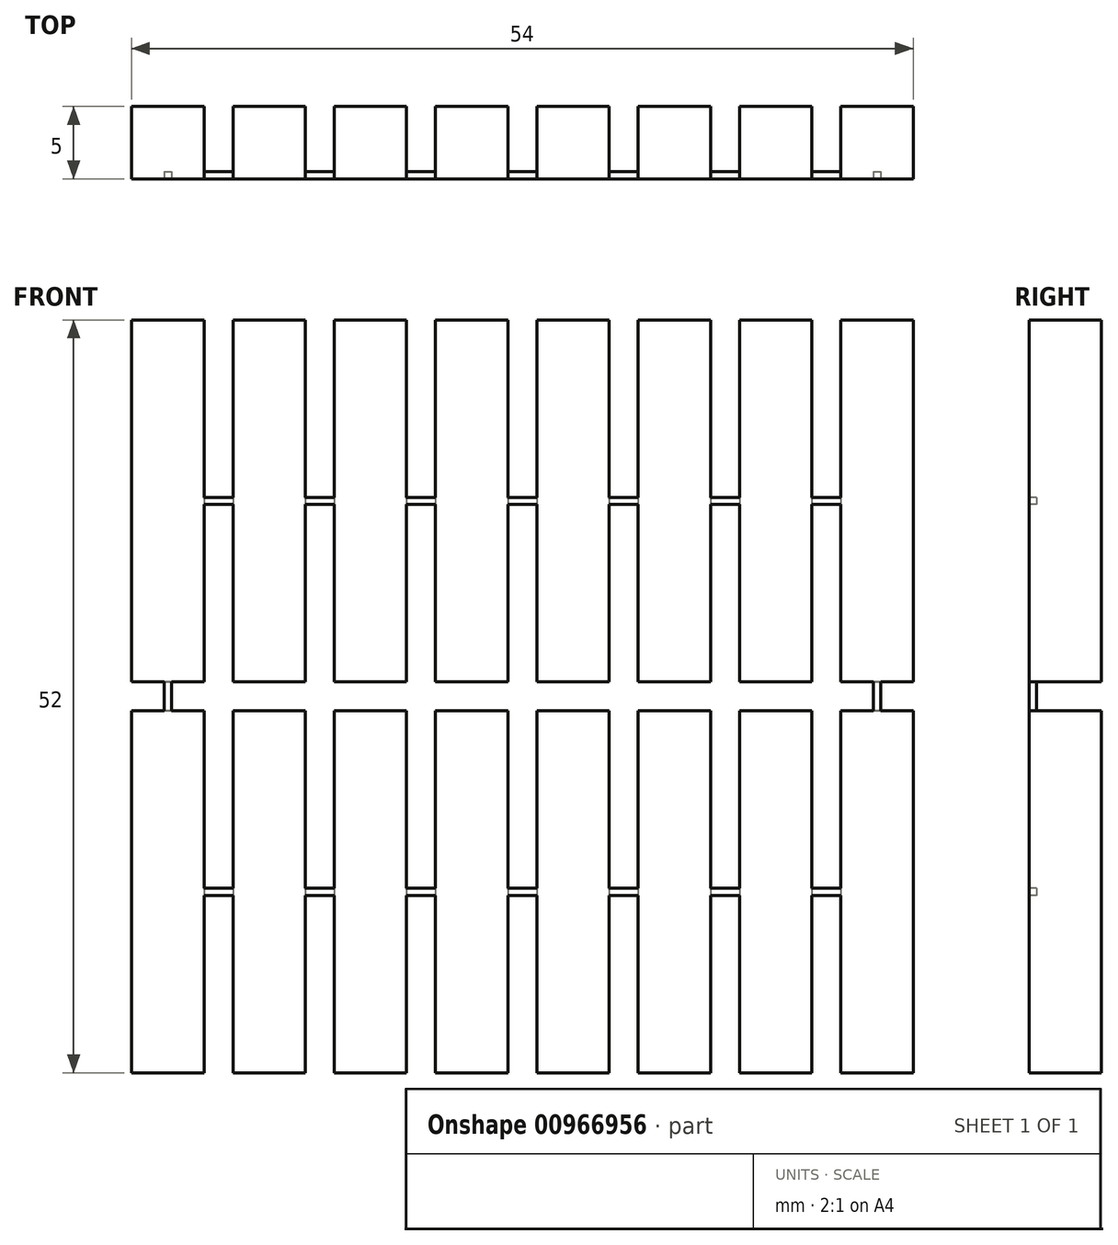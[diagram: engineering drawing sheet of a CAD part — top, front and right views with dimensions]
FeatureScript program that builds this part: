
annotation { "Feature Type Name" : "Feature", "Feature Type Description" : "" }
export const myFeature = defineFeature(function(context is Context, id is Id, definition is map)
    precondition{}
    {
        {
            var Q0;
            Q0=qCreatedBy(makeId("Front.planeOp"),FACE);
            var sketch = newSketch(context, id + "F0", { "sketchPlane" : qUnion([Q0])});
            skLineSegment(sketch, "E0.bottom", {"start": v(2.5, -12.5) * mm, "end": v(-2.5, -12.5) * mm});
            skLineSegment(sketch, "E0.top", {"start": v(2.5, 12.5) * mm, "end": v(-2.5, 12.5) * mm});
            skLineSegment(sketch, "E0.left", {"start": v(2.5, -12.5) * mm, "end": v(2.5, 12.5) * mm});
            skLineSegment(sketch, "E0.right", {"start": v(-2.5, -12.5) * mm, "end": v(-2.5, 12.5) * mm});
            skPoint(sketch, "E0.middle", {"position": v(0, 0) * mm});
            skLineSegment(sketch, "E1.top", {"start": v(0.25, 14.5) * mm, "end": v(-0.25, 14.5) * mm});
            skPoint(sketch, "E1.middle", {"position": v(0, 12.5) * mm});
            skLineSegment(sketch, "E2", {"start": v(-0.25, 14.5) * mm, "end": v(-0.25, 12.5) * mm});
            skLineSegment(sketch, "E3", {"start": v(0.25, 14.5) * mm, "end": v(0.25, 12.5) * mm});
            skLineSegment(sketch, "E4", {"start": v(0.25, 12.5) * mm, "end": v(-0.25, 12.5) * mm});
            skPoint(sketch, "E5", {"position": v(0, 14.5) * mm});
            skPoint(sketch, "E6", {"position": v(2.5, 0) * mm});
            skLineSegment(sketch, "E7.right", {"start": v(4.5, -0.25) * mm, "end": v(4.5, 0.25) * mm});
            skLineSegment(sketch, "E8", {"start": v(4.5, 0.25) * mm, "end": v(2.5, 0.25) * mm});
            skLineSegment(sketch, "E9", {"start": v(4.5, -0.25) * mm, "end": v(2.5, -0.25) * mm});
            skLineSegment(sketch, "E10", {"start": v(2.5, -0.25) * mm, "end": v(2.5, 0.25) * mm});
            skPoint(sketch, "E11", {"position": v(4.5, 0) * mm});
            skLineSegment(sketch, "E12.0.1.0", {"start": v(4.5, 27.25) * mm, "end": v(2.5, 27.25) * mm});
            skLineSegment(sketch, "E12.0.1.1", {"start": v(2.5, 14.5) * mm, "end": v(2.5, 39.5) * mm});
            skLineSegment(sketch, "E12.0.1.2", {"start": v(0.25, 41.5) * mm, "end": v(0.25, 39.5) * mm});
            skPoint(sketch, "E12.0.1.3", {"position": v(2.5, 27) * mm});
            skLineSegment(sketch, "E12.0.1.4", {"start": v(-0.25, 41.5) * mm, "end": v(-0.25, 39.5) * mm});
            skLineSegment(sketch, "E12.0.1.5", {"start": v(2.5, 39.5) * mm, "end": v(-2.5, 39.5) * mm});
            skPoint(sketch, "E12.0.1.6", {"position": v(0, 27) * mm});
            skLineSegment(sketch, "E12.0.1.7", {"start": v(2.5, 14.5) * mm, "end": v(-2.5, 14.5) * mm});
            skLineSegment(sketch, "E12.0.1.8", {"start": v(4.5, 26.75) * mm, "end": v(2.5, 26.75) * mm});
            skPoint(sketch, "E12.0.1.9", {"position": v(4.5, 27) * mm});
            skLineSegment(sketch, "E12.0.1.10", {"start": v(-2.5, 14.5) * mm, "end": v(-2.5, 39.5) * mm});
            skPoint(sketch, "E12.0.1.11", {"position": v(0, 39.5) * mm});
            skPoint(sketch, "E12.0.1.12", {"position": v(0, 41.5) * mm});
            skPoint(sketch, "E12.0.1.13", {"position": v(4.5, 27) * mm});
            skPoint(sketch, "E12.0.1.14", {"position": v(0, 41.5) * mm});
            skPoint(sketch, "E12.0.1.15", {"position": v(2.5, 27) * mm});
            skLineSegment(sketch, "E12.0.1.16", {"start": v(0.25, 41.5) * mm, "end": v(-0.25, 41.5) * mm});
            skLineSegment(sketch, "E12.0.1.17", {"start": v(4.5, 26.75) * mm, "end": v(4.5, 27.25) * mm});
            skLineSegment(sketch, "E12.0.1.18", {"start": v(2.5, 26.75) * mm, "end": v(2.5, 27.25) * mm});
            skLineSegment(sketch, "E12.0.1.19", {"start": v(0.25, 39.5) * mm, "end": v(-0.25, 39.5) * mm});
            skLineSegment(sketch, "E12.1.0.0", {"start": v(11.5, 0.25) * mm, "end": v(9.5, 0.25) * mm});
            skLineSegment(sketch, "E12.1.0.1", {"start": v(9.5, -12.5) * mm, "end": v(9.5, 12.5) * mm});
            skLineSegment(sketch, "E12.1.0.2", {"start": v(7.25, 14.5) * mm, "end": v(7.25, 12.5) * mm});
            skPoint(sketch, "E12.1.0.3", {"position": v(9.5, 0) * mm});
            skLineSegment(sketch, "E12.1.0.4", {"start": v(6.75, 14.5) * mm, "end": v(6.75, 12.5) * mm});
            skLineSegment(sketch, "E12.1.0.5", {"start": v(9.5, 12.5) * mm, "end": v(4.5, 12.5) * mm});
            skPoint(sketch, "E12.1.0.6", {"position": v(7, 0) * mm});
            skLineSegment(sketch, "E12.1.0.7", {"start": v(9.5, -12.5) * mm, "end": v(4.5, -12.5) * mm});
            skLineSegment(sketch, "E12.1.0.8", {"start": v(11.5, -0.25) * mm, "end": v(9.5, -0.25) * mm});
            skPoint(sketch, "E12.1.0.9", {"position": v(11.5, 0) * mm});
            skLineSegment(sketch, "E12.1.0.10", {"start": v(4.5, -12.5) * mm, "end": v(4.5, 12.5) * mm});
            skPoint(sketch, "E12.1.0.11", {"position": v(7, 12.5) * mm});
            skPoint(sketch, "E12.1.0.12", {"position": v(7, 14.5) * mm});
            skPoint(sketch, "E12.1.0.13", {"position": v(11.5, 0) * mm});
            skPoint(sketch, "E12.1.0.14", {"position": v(7, 14.5) * mm});
            skPoint(sketch, "E12.1.0.15", {"position": v(9.5, 0) * mm});
            skLineSegment(sketch, "E12.1.0.16", {"start": v(7.25, 14.5) * mm, "end": v(6.75, 14.5) * mm});
            skLineSegment(sketch, "E12.1.0.17", {"start": v(11.5, -0.25) * mm, "end": v(11.5, 0.25) * mm});
            skLineSegment(sketch, "E12.1.0.18", {"start": v(9.5, -0.25) * mm, "end": v(9.5, 0.25) * mm});
            skLineSegment(sketch, "E12.1.0.19", {"start": v(7.25, 12.5) * mm, "end": v(6.75, 12.5) * mm});
            skLineSegment(sketch, "E12.1.1.0", {"start": v(11.5, 27.25) * mm, "end": v(9.5, 27.25) * mm});
            skLineSegment(sketch, "E12.1.1.1", {"start": v(9.5, 14.5) * mm, "end": v(9.5, 39.5) * mm});
            skLineSegment(sketch, "E12.1.1.2", {"start": v(7.25, 41.5) * mm, "end": v(7.25, 39.5) * mm});
            skPoint(sketch, "E12.1.1.3", {"position": v(9.5, 27) * mm});
            skLineSegment(sketch, "E12.1.1.4", {"start": v(6.75, 41.5) * mm, "end": v(6.75, 39.5) * mm});
            skLineSegment(sketch, "E12.1.1.5", {"start": v(9.5, 39.5) * mm, "end": v(4.5, 39.5) * mm});
            skPoint(sketch, "E12.1.1.6", {"position": v(7, 27) * mm});
            skLineSegment(sketch, "E12.1.1.7", {"start": v(9.5, 14.5) * mm, "end": v(4.5, 14.5) * mm});
            skLineSegment(sketch, "E12.1.1.8", {"start": v(11.5, 26.75) * mm, "end": v(9.5, 26.75) * mm});
            skPoint(sketch, "E12.1.1.9", {"position": v(11.5, 27) * mm});
            skLineSegment(sketch, "E12.1.1.10", {"start": v(4.5, 14.5) * mm, "end": v(4.5, 39.5) * mm});
            skPoint(sketch, "E12.1.1.11", {"position": v(7, 39.5) * mm});
            skPoint(sketch, "E12.1.1.12", {"position": v(7, 41.5) * mm});
            skPoint(sketch, "E12.1.1.13", {"position": v(11.5, 27) * mm});
            skPoint(sketch, "E12.1.1.14", {"position": v(7, 41.5) * mm});
            skPoint(sketch, "E12.1.1.15", {"position": v(9.5, 27) * mm});
            skLineSegment(sketch, "E12.1.1.16", {"start": v(7.25, 41.5) * mm, "end": v(6.75, 41.5) * mm});
            skLineSegment(sketch, "E12.1.1.17", {"start": v(11.5, 26.75) * mm, "end": v(11.5, 27.25) * mm});
            skLineSegment(sketch, "E12.1.1.18", {"start": v(9.5, 26.75) * mm, "end": v(9.5, 27.25) * mm});
            skLineSegment(sketch, "E12.1.1.19", {"start": v(7.25, 39.5) * mm, "end": v(6.75, 39.5) * mm});
            skLineSegment(sketch, "E12.2.0.0", {"start": v(18.5, 0.25) * mm, "end": v(16.5, 0.25) * mm});
            skLineSegment(sketch, "E12.2.0.1", {"start": v(16.5, -12.5) * mm, "end": v(16.5, 12.5) * mm});
            skLineSegment(sketch, "E12.2.0.2", {"start": v(14.25, 14.5) * mm, "end": v(14.25, 12.5) * mm});
            skPoint(sketch, "E12.2.0.3", {"position": v(16.5, 0) * mm});
            skLineSegment(sketch, "E12.2.0.4", {"start": v(13.75, 14.5) * mm, "end": v(13.75, 12.5) * mm});
            skLineSegment(sketch, "E12.2.0.5", {"start": v(16.5, 12.5) * mm, "end": v(11.5, 12.5) * mm});
            skPoint(sketch, "E12.2.0.6", {"position": v(14, 0) * mm});
            skLineSegment(sketch, "E12.2.0.7", {"start": v(16.5, -12.5) * mm, "end": v(11.5, -12.5) * mm});
            skLineSegment(sketch, "E12.2.0.8", {"start": v(18.5, -0.25) * mm, "end": v(16.5, -0.25) * mm});
            skPoint(sketch, "E12.2.0.9", {"position": v(18.5, 0) * mm});
            skLineSegment(sketch, "E12.2.0.10", {"start": v(11.5, -12.5) * mm, "end": v(11.5, 12.5) * mm});
            skPoint(sketch, "E12.2.0.11", {"position": v(14, 12.5) * mm});
            skPoint(sketch, "E12.2.0.12", {"position": v(14, 14.5) * mm});
            skPoint(sketch, "E12.2.0.13", {"position": v(18.5, 0) * mm});
            skPoint(sketch, "E12.2.0.14", {"position": v(14, 14.5) * mm});
            skPoint(sketch, "E12.2.0.15", {"position": v(16.5, 0) * mm});
            skLineSegment(sketch, "E12.2.0.16", {"start": v(14.25, 14.5) * mm, "end": v(13.75, 14.5) * mm});
            skLineSegment(sketch, "E12.2.0.17", {"start": v(18.5, -0.25) * mm, "end": v(18.5, 0.25) * mm});
            skLineSegment(sketch, "E12.2.0.18", {"start": v(16.5, -0.25) * mm, "end": v(16.5, 0.25) * mm});
            skLineSegment(sketch, "E12.2.0.19", {"start": v(14.25, 12.5) * mm, "end": v(13.75, 12.5) * mm});
            skLineSegment(sketch, "E12.2.1.0", {"start": v(18.5, 27.25) * mm, "end": v(16.5, 27.25) * mm});
            skLineSegment(sketch, "E12.2.1.1", {"start": v(16.5, 14.5) * mm, "end": v(16.5, 39.5) * mm});
            skLineSegment(sketch, "E12.2.1.2", {"start": v(14.25, 41.5) * mm, "end": v(14.25, 39.5) * mm});
            skPoint(sketch, "E12.2.1.3", {"position": v(16.5, 27) * mm});
            skLineSegment(sketch, "E12.2.1.4", {"start": v(13.75, 41.5) * mm, "end": v(13.75, 39.5) * mm});
            skLineSegment(sketch, "E12.2.1.5", {"start": v(16.5, 39.5) * mm, "end": v(11.5, 39.5) * mm});
            skPoint(sketch, "E12.2.1.6", {"position": v(14, 27) * mm});
            skLineSegment(sketch, "E12.2.1.7", {"start": v(16.5, 14.5) * mm, "end": v(11.5, 14.5) * mm});
            skLineSegment(sketch, "E12.2.1.8", {"start": v(18.5, 26.75) * mm, "end": v(16.5, 26.75) * mm});
            skPoint(sketch, "E12.2.1.9", {"position": v(18.5, 27) * mm});
            skLineSegment(sketch, "E12.2.1.10", {"start": v(11.5, 14.5) * mm, "end": v(11.5, 39.5) * mm});
            skPoint(sketch, "E12.2.1.11", {"position": v(14, 39.5) * mm});
            skPoint(sketch, "E12.2.1.12", {"position": v(14, 41.5) * mm});
            skPoint(sketch, "E12.2.1.13", {"position": v(18.5, 27) * mm});
            skPoint(sketch, "E12.2.1.14", {"position": v(14, 41.5) * mm});
            skPoint(sketch, "E12.2.1.15", {"position": v(16.5, 27) * mm});
            skLineSegment(sketch, "E12.2.1.16", {"start": v(14.25, 41.5) * mm, "end": v(13.75, 41.5) * mm});
            skLineSegment(sketch, "E12.2.1.17", {"start": v(18.5, 26.75) * mm, "end": v(18.5, 27.25) * mm});
            skLineSegment(sketch, "E12.2.1.18", {"start": v(16.5, 26.75) * mm, "end": v(16.5, 27.25) * mm});
            skLineSegment(sketch, "E12.2.1.19", {"start": v(14.25, 39.5) * mm, "end": v(13.75, 39.5) * mm});
            skLineSegment(sketch, "E12.3.0.0", {"start": v(25.5, 0.25) * mm, "end": v(23.5, 0.25) * mm});
            skLineSegment(sketch, "E12.3.0.1", {"start": v(23.5, -12.5) * mm, "end": v(23.5, 12.5) * mm});
            skLineSegment(sketch, "E12.3.0.2", {"start": v(21.25, 14.5) * mm, "end": v(21.25, 12.5) * mm});
            skPoint(sketch, "E12.3.0.3", {"position": v(23.5, 0) * mm});
            skLineSegment(sketch, "E12.3.0.4", {"start": v(20.75, 14.5) * mm, "end": v(20.75, 12.5) * mm});
            skLineSegment(sketch, "E12.3.0.5", {"start": v(23.5, 12.5) * mm, "end": v(18.5, 12.5) * mm});
            skPoint(sketch, "E12.3.0.6", {"position": v(21, 0) * mm});
            skLineSegment(sketch, "E12.3.0.7", {"start": v(23.5, -12.5) * mm, "end": v(18.5, -12.5) * mm});
            skLineSegment(sketch, "E12.3.0.8", {"start": v(25.5, -0.25) * mm, "end": v(23.5, -0.25) * mm});
            skPoint(sketch, "E12.3.0.9", {"position": v(25.5, 0) * mm});
            skLineSegment(sketch, "E12.3.0.10", {"start": v(18.5, -12.5) * mm, "end": v(18.5, 12.5) * mm});
            skPoint(sketch, "E12.3.0.11", {"position": v(21, 12.5) * mm});
            skPoint(sketch, "E12.3.0.12", {"position": v(21, 14.5) * mm});
            skPoint(sketch, "E12.3.0.13", {"position": v(25.5, 0) * mm});
            skPoint(sketch, "E12.3.0.14", {"position": v(21, 14.5) * mm});
            skPoint(sketch, "E12.3.0.15", {"position": v(23.5, 0) * mm});
            skLineSegment(sketch, "E12.3.0.16", {"start": v(21.25, 14.5) * mm, "end": v(20.75, 14.5) * mm});
            skLineSegment(sketch, "E12.3.0.17", {"start": v(25.5, -0.25) * mm, "end": v(25.5, 0.25) * mm});
            skLineSegment(sketch, "E12.3.0.18", {"start": v(23.5, -0.25) * mm, "end": v(23.5, 0.25) * mm});
            skLineSegment(sketch, "E12.3.0.19", {"start": v(21.25, 12.5) * mm, "end": v(20.75, 12.5) * mm});
            skLineSegment(sketch, "E12.3.1.0", {"start": v(25.5, 27.25) * mm, "end": v(23.5, 27.25) * mm});
            skLineSegment(sketch, "E12.3.1.1", {"start": v(23.5, 14.5) * mm, "end": v(23.5, 39.5) * mm});
            skLineSegment(sketch, "E12.3.1.2", {"start": v(21.25, 41.5) * mm, "end": v(21.25, 39.5) * mm});
            skPoint(sketch, "E12.3.1.3", {"position": v(23.5, 27) * mm});
            skLineSegment(sketch, "E12.3.1.4", {"start": v(20.75, 41.5) * mm, "end": v(20.75, 39.5) * mm});
            skLineSegment(sketch, "E12.3.1.5", {"start": v(23.5, 39.5) * mm, "end": v(18.5, 39.5) * mm});
            skPoint(sketch, "E12.3.1.6", {"position": v(21, 27) * mm});
            skLineSegment(sketch, "E12.3.1.7", {"start": v(23.5, 14.5) * mm, "end": v(18.5, 14.5) * mm});
            skLineSegment(sketch, "E12.3.1.8", {"start": v(25.5, 26.75) * mm, "end": v(23.5, 26.75) * mm});
            skPoint(sketch, "E12.3.1.9", {"position": v(25.5, 27) * mm});
            skLineSegment(sketch, "E12.3.1.10", {"start": v(18.5, 14.5) * mm, "end": v(18.5, 39.5) * mm});
            skPoint(sketch, "E12.3.1.11", {"position": v(21, 39.5) * mm});
            skPoint(sketch, "E12.3.1.12", {"position": v(21, 41.5) * mm});
            skPoint(sketch, "E12.3.1.13", {"position": v(25.5, 27) * mm});
            skPoint(sketch, "E12.3.1.14", {"position": v(21, 41.5) * mm});
            skPoint(sketch, "E12.3.1.15", {"position": v(23.5, 27) * mm});
            skLineSegment(sketch, "E12.3.1.16", {"start": v(21.25, 41.5) * mm, "end": v(20.75, 41.5) * mm});
            skLineSegment(sketch, "E12.3.1.17", {"start": v(25.5, 26.75) * mm, "end": v(25.5, 27.25) * mm});
            skLineSegment(sketch, "E12.3.1.18", {"start": v(23.5, 26.75) * mm, "end": v(23.5, 27.25) * mm});
            skLineSegment(sketch, "E12.3.1.19", {"start": v(21.25, 39.5) * mm, "end": v(20.75, 39.5) * mm});
            skLineSegment(sketch, "E12.4.0.0", {"start": v(32.5, 0.25) * mm, "end": v(30.5, 0.25) * mm});
            skLineSegment(sketch, "E12.4.0.1", {"start": v(30.5, -12.5) * mm, "end": v(30.5, 12.5) * mm});
            skLineSegment(sketch, "E12.4.0.2", {"start": v(28.25, 14.5) * mm, "end": v(28.25, 12.5) * mm});
            skPoint(sketch, "E12.4.0.3", {"position": v(30.5, 0) * mm});
            skLineSegment(sketch, "E12.4.0.4", {"start": v(27.75, 14.5) * mm, "end": v(27.75, 12.5) * mm});
            skLineSegment(sketch, "E12.4.0.5", {"start": v(30.5, 12.5) * mm, "end": v(25.5, 12.5) * mm});
            skPoint(sketch, "E12.4.0.6", {"position": v(28, 0) * mm});
            skLineSegment(sketch, "E12.4.0.7", {"start": v(30.5, -12.5) * mm, "end": v(25.5, -12.5) * mm});
            skLineSegment(sketch, "E12.4.0.8", {"start": v(32.5, -0.25) * mm, "end": v(30.5, -0.25) * mm});
            skPoint(sketch, "E12.4.0.9", {"position": v(32.5, 0) * mm});
            skLineSegment(sketch, "E12.4.0.10", {"start": v(25.5, -12.5) * mm, "end": v(25.5, 12.5) * mm});
            skPoint(sketch, "E12.4.0.11", {"position": v(28, 12.5) * mm});
            skPoint(sketch, "E12.4.0.12", {"position": v(28, 14.5) * mm});
            skPoint(sketch, "E12.4.0.13", {"position": v(32.5, 0) * mm});
            skPoint(sketch, "E12.4.0.14", {"position": v(28, 14.5) * mm});
            skPoint(sketch, "E12.4.0.15", {"position": v(30.5, 0) * mm});
            skLineSegment(sketch, "E12.4.0.16", {"start": v(28.25, 14.5) * mm, "end": v(27.75, 14.5) * mm});
            skLineSegment(sketch, "E12.4.0.17", {"start": v(32.5, -0.25) * mm, "end": v(32.5, 0.25) * mm});
            skLineSegment(sketch, "E12.4.0.18", {"start": v(30.5, -0.25) * mm, "end": v(30.5, 0.25) * mm});
            skLineSegment(sketch, "E12.4.0.19", {"start": v(28.25, 12.5) * mm, "end": v(27.75, 12.5) * mm});
            skLineSegment(sketch, "E12.4.1.0", {"start": v(32.5, 27.25) * mm, "end": v(30.5, 27.25) * mm});
            skLineSegment(sketch, "E12.4.1.1", {"start": v(30.5, 14.5) * mm, "end": v(30.5, 39.5) * mm});
            skLineSegment(sketch, "E12.4.1.2", {"start": v(28.25, 41.5) * mm, "end": v(28.25, 39.5) * mm});
            skPoint(sketch, "E12.4.1.3", {"position": v(30.5, 27) * mm});
            skLineSegment(sketch, "E12.4.1.4", {"start": v(27.75, 41.5) * mm, "end": v(27.75, 39.5) * mm});
            skLineSegment(sketch, "E12.4.1.5", {"start": v(30.5, 39.5) * mm, "end": v(25.5, 39.5) * mm});
            skPoint(sketch, "E12.4.1.6", {"position": v(28, 27) * mm});
            skLineSegment(sketch, "E12.4.1.7", {"start": v(30.5, 14.5) * mm, "end": v(25.5, 14.5) * mm});
            skLineSegment(sketch, "E12.4.1.8", {"start": v(32.5, 26.75) * mm, "end": v(30.5, 26.75) * mm});
            skPoint(sketch, "E12.4.1.9", {"position": v(32.5, 27) * mm});
            skLineSegment(sketch, "E12.4.1.10", {"start": v(25.5, 14.5) * mm, "end": v(25.5, 39.5) * mm});
            skPoint(sketch, "E12.4.1.11", {"position": v(28, 39.5) * mm});
            skPoint(sketch, "E12.4.1.12", {"position": v(28, 41.5) * mm});
            skPoint(sketch, "E12.4.1.13", {"position": v(32.5, 27) * mm});
            skPoint(sketch, "E12.4.1.14", {"position": v(28, 41.5) * mm});
            skPoint(sketch, "E12.4.1.15", {"position": v(30.5, 27) * mm});
            skLineSegment(sketch, "E12.4.1.16", {"start": v(28.25, 41.5) * mm, "end": v(27.75, 41.5) * mm});
            skLineSegment(sketch, "E12.4.1.17", {"start": v(32.5, 26.75) * mm, "end": v(32.5, 27.25) * mm});
            skLineSegment(sketch, "E12.4.1.18", {"start": v(30.5, 26.75) * mm, "end": v(30.5, 27.25) * mm});
            skLineSegment(sketch, "E12.4.1.19", {"start": v(28.25, 39.5) * mm, "end": v(27.75, 39.5) * mm});
            skLineSegment(sketch, "E12.5.0.0", {"start": v(39.5, 0.25) * mm, "end": v(37.5, 0.25) * mm});
            skLineSegment(sketch, "E12.5.0.1", {"start": v(37.5, -12.5) * mm, "end": v(37.5, 12.5) * mm});
            skLineSegment(sketch, "E12.5.0.2", {"start": v(35.25, 14.5) * mm, "end": v(35.25, 12.5) * mm});
            skPoint(sketch, "E12.5.0.3", {"position": v(37.5, 0) * mm});
            skLineSegment(sketch, "E12.5.0.4", {"start": v(34.75, 14.5) * mm, "end": v(34.75, 12.5) * mm});
            skLineSegment(sketch, "E12.5.0.5", {"start": v(37.5, 12.5) * mm, "end": v(32.5, 12.5) * mm});
            skPoint(sketch, "E12.5.0.6", {"position": v(35, 0) * mm});
            skLineSegment(sketch, "E12.5.0.7", {"start": v(37.5, -12.5) * mm, "end": v(32.5, -12.5) * mm});
            skLineSegment(sketch, "E12.5.0.8", {"start": v(39.5, -0.25) * mm, "end": v(37.5, -0.25) * mm});
            skPoint(sketch, "E12.5.0.9", {"position": v(39.5, 0) * mm});
            skLineSegment(sketch, "E12.5.0.10", {"start": v(32.5, -12.5) * mm, "end": v(32.5, 12.5) * mm});
            skPoint(sketch, "E12.5.0.11", {"position": v(35, 12.5) * mm});
            skPoint(sketch, "E12.5.0.12", {"position": v(35, 14.5) * mm});
            skPoint(sketch, "E12.5.0.13", {"position": v(39.5, 0) * mm});
            skPoint(sketch, "E12.5.0.14", {"position": v(35, 14.5) * mm});
            skPoint(sketch, "E12.5.0.15", {"position": v(37.5, 0) * mm});
            skLineSegment(sketch, "E12.5.0.16", {"start": v(35.25, 14.5) * mm, "end": v(34.75, 14.5) * mm});
            skLineSegment(sketch, "E12.5.0.17", {"start": v(39.5, -0.25) * mm, "end": v(39.5, 0.25) * mm});
            skLineSegment(sketch, "E12.5.0.18", {"start": v(37.5, -0.25) * mm, "end": v(37.5, 0.25) * mm});
            skLineSegment(sketch, "E12.5.0.19", {"start": v(35.25, 12.5) * mm, "end": v(34.75, 12.5) * mm});
            skLineSegment(sketch, "E12.5.1.0", {"start": v(39.5, 27.25) * mm, "end": v(37.5, 27.25) * mm});
            skLineSegment(sketch, "E12.5.1.1", {"start": v(37.5, 14.5) * mm, "end": v(37.5, 39.5) * mm});
            skLineSegment(sketch, "E12.5.1.2", {"start": v(35.25, 41.5) * mm, "end": v(35.25, 39.5) * mm});
            skPoint(sketch, "E12.5.1.3", {"position": v(37.5, 27) * mm});
            skLineSegment(sketch, "E12.5.1.4", {"start": v(34.75, 41.5) * mm, "end": v(34.75, 39.5) * mm});
            skLineSegment(sketch, "E12.5.1.5", {"start": v(37.5, 39.5) * mm, "end": v(32.5, 39.5) * mm});
            skPoint(sketch, "E12.5.1.6", {"position": v(35, 27) * mm});
            skLineSegment(sketch, "E12.5.1.7", {"start": v(37.5, 14.5) * mm, "end": v(32.5, 14.5) * mm});
            skLineSegment(sketch, "E12.5.1.8", {"start": v(39.5, 26.75) * mm, "end": v(37.5, 26.75) * mm});
            skPoint(sketch, "E12.5.1.9", {"position": v(39.5, 27) * mm});
            skLineSegment(sketch, "E12.5.1.10", {"start": v(32.5, 14.5) * mm, "end": v(32.5, 39.5) * mm});
            skPoint(sketch, "E12.5.1.11", {"position": v(35, 39.5) * mm});
            skPoint(sketch, "E12.5.1.12", {"position": v(35, 41.5) * mm});
            skPoint(sketch, "E12.5.1.13", {"position": v(39.5, 27) * mm});
            skPoint(sketch, "E12.5.1.14", {"position": v(35, 41.5) * mm});
            skPoint(sketch, "E12.5.1.15", {"position": v(37.5, 27) * mm});
            skLineSegment(sketch, "E12.5.1.16", {"start": v(35.25, 41.5) * mm, "end": v(34.75, 41.5) * mm});
            skLineSegment(sketch, "E12.5.1.17", {"start": v(39.5, 26.75) * mm, "end": v(39.5, 27.25) * mm});
            skLineSegment(sketch, "E12.5.1.18", {"start": v(37.5, 26.75) * mm, "end": v(37.5, 27.25) * mm});
            skLineSegment(sketch, "E12.5.1.19", {"start": v(35.25, 39.5) * mm, "end": v(34.75, 39.5) * mm});
            skLineSegment(sketch, "E12.6.0.0", {"start": v(46.5, 0.25) * mm, "end": v(44.5, 0.25) * mm});
            skLineSegment(sketch, "E12.6.0.1", {"start": v(44.5, -12.5) * mm, "end": v(44.5, 12.5) * mm});
            skLineSegment(sketch, "E12.6.0.2", {"start": v(42.25, 14.5) * mm, "end": v(42.25, 12.5) * mm});
            skPoint(sketch, "E12.6.0.3", {"position": v(44.5, 0) * mm});
            skLineSegment(sketch, "E12.6.0.4", {"start": v(41.75, 14.5) * mm, "end": v(41.75, 12.5) * mm});
            skLineSegment(sketch, "E12.6.0.5", {"start": v(44.5, 12.5) * mm, "end": v(39.5, 12.5) * mm});
            skPoint(sketch, "E12.6.0.6", {"position": v(42, 0) * mm});
            skLineSegment(sketch, "E12.6.0.7", {"start": v(44.5, -12.5) * mm, "end": v(39.5, -12.5) * mm});
            skLineSegment(sketch, "E12.6.0.8", {"start": v(46.5, -0.25) * mm, "end": v(44.5, -0.25) * mm});
            skPoint(sketch, "E12.6.0.9", {"position": v(46.5, 0) * mm});
            skLineSegment(sketch, "E12.6.0.10", {"start": v(39.5, -12.5) * mm, "end": v(39.5, 12.5) * mm});
            skPoint(sketch, "E12.6.0.11", {"position": v(42, 12.5) * mm});
            skPoint(sketch, "E12.6.0.12", {"position": v(42, 14.5) * mm});
            skPoint(sketch, "E12.6.0.13", {"position": v(46.5, 0) * mm});
            skPoint(sketch, "E12.6.0.14", {"position": v(42, 14.5) * mm});
            skPoint(sketch, "E12.6.0.15", {"position": v(44.5, 0) * mm});
            skLineSegment(sketch, "E12.6.0.16", {"start": v(42.25, 14.5) * mm, "end": v(41.75, 14.5) * mm});
            skLineSegment(sketch, "E12.6.0.17", {"start": v(46.5, -0.25) * mm, "end": v(46.5, 0.25) * mm});
            skLineSegment(sketch, "E12.6.0.18", {"start": v(44.5, -0.25) * mm, "end": v(44.5, 0.25) * mm});
            skLineSegment(sketch, "E12.6.0.19", {"start": v(42.25, 12.5) * mm, "end": v(41.75, 12.5) * mm});
            skLineSegment(sketch, "E12.6.1.0", {"start": v(46.5, 27.25) * mm, "end": v(44.5, 27.25) * mm});
            skLineSegment(sketch, "E12.6.1.1", {"start": v(44.5, 14.5) * mm, "end": v(44.5, 39.5) * mm});
            skLineSegment(sketch, "E12.6.1.2", {"start": v(42.25, 41.5) * mm, "end": v(42.25, 39.5) * mm});
            skPoint(sketch, "E12.6.1.3", {"position": v(44.5, 27) * mm});
            skLineSegment(sketch, "E12.6.1.4", {"start": v(41.75, 41.5) * mm, "end": v(41.75, 39.5) * mm});
            skLineSegment(sketch, "E12.6.1.5", {"start": v(44.5, 39.5) * mm, "end": v(39.5, 39.5) * mm});
            skPoint(sketch, "E12.6.1.6", {"position": v(42, 27) * mm});
            skLineSegment(sketch, "E12.6.1.7", {"start": v(44.5, 14.5) * mm, "end": v(39.5, 14.5) * mm});
            skLineSegment(sketch, "E12.6.1.8", {"start": v(46.5, 26.75) * mm, "end": v(44.5, 26.75) * mm});
            skPoint(sketch, "E12.6.1.9", {"position": v(46.5, 27) * mm});
            skLineSegment(sketch, "E12.6.1.10", {"start": v(39.5, 14.5) * mm, "end": v(39.5, 39.5) * mm});
            skPoint(sketch, "E12.6.1.11", {"position": v(42, 39.5) * mm});
            skPoint(sketch, "E12.6.1.12", {"position": v(42, 41.5) * mm});
            skPoint(sketch, "E12.6.1.13", {"position": v(46.5, 27) * mm});
            skPoint(sketch, "E12.6.1.14", {"position": v(42, 41.5) * mm});
            skPoint(sketch, "E12.6.1.15", {"position": v(44.5, 27) * mm});
            skLineSegment(sketch, "E12.6.1.16", {"start": v(42.25, 41.5) * mm, "end": v(41.75, 41.5) * mm});
            skLineSegment(sketch, "E12.6.1.17", {"start": v(46.5, 26.75) * mm, "end": v(46.5, 27.25) * mm});
            skLineSegment(sketch, "E12.6.1.18", {"start": v(44.5, 26.75) * mm, "end": v(44.5, 27.25) * mm});
            skLineSegment(sketch, "E12.6.1.19", {"start": v(42.25, 39.5) * mm, "end": v(41.75, 39.5) * mm});
            skLineSegment(sketch, "E12.7.0.0", {"start": v(53.5, 0.25) * mm, "end": v(51.5, 0.25) * mm});
            skLineSegment(sketch, "E12.7.0.1", {"start": v(51.5, -12.5) * mm, "end": v(51.5, 12.5) * mm});
            skLineSegment(sketch, "E12.7.0.2", {"start": v(49.25, 14.5) * mm, "end": v(49.25, 12.5) * mm});
            skPoint(sketch, "E12.7.0.3", {"position": v(51.5, 0) * mm});
            skLineSegment(sketch, "E12.7.0.4", {"start": v(48.75, 14.5) * mm, "end": v(48.75, 12.5) * mm});
            skLineSegment(sketch, "E12.7.0.5", {"start": v(51.5, 12.5) * mm, "end": v(46.5, 12.5) * mm});
            skPoint(sketch, "E12.7.0.6", {"position": v(49, 0) * mm});
            skLineSegment(sketch, "E12.7.0.7", {"start": v(51.5, -12.5) * mm, "end": v(46.5, -12.5) * mm});
            skLineSegment(sketch, "E12.7.0.8", {"start": v(53.5, -0.25) * mm, "end": v(51.5, -0.25) * mm});
            skPoint(sketch, "E12.7.0.9", {"position": v(53.5, 0) * mm});
            skLineSegment(sketch, "E12.7.0.10", {"start": v(46.5, -12.5) * mm, "end": v(46.5, 12.5) * mm});
            skPoint(sketch, "E12.7.0.11", {"position": v(49, 12.5) * mm});
            skPoint(sketch, "E12.7.0.12", {"position": v(49, 14.5) * mm});
            skPoint(sketch, "E12.7.0.13", {"position": v(53.5, 0) * mm});
            skPoint(sketch, "E12.7.0.14", {"position": v(49, 14.5) * mm});
            skPoint(sketch, "E12.7.0.15", {"position": v(51.5, 0) * mm});
            skLineSegment(sketch, "E12.7.0.16", {"start": v(49.25, 14.5) * mm, "end": v(48.75, 14.5) * mm});
            skLineSegment(sketch, "E12.7.0.17", {"start": v(53.5, -0.25) * mm, "end": v(53.5, 0.25) * mm});
            skLineSegment(sketch, "E12.7.0.18", {"start": v(51.5, -0.25) * mm, "end": v(51.5, 0.25) * mm});
            skLineSegment(sketch, "E12.7.0.19", {"start": v(49.25, 12.5) * mm, "end": v(48.75, 12.5) * mm});
            skLineSegment(sketch, "E12.7.1.0", {"start": v(53.5, 27.25) * mm, "end": v(51.5, 27.25) * mm});
            skLineSegment(sketch, "E12.7.1.1", {"start": v(51.5, 14.5) * mm, "end": v(51.5, 39.5) * mm});
            skLineSegment(sketch, "E12.7.1.2", {"start": v(49.25, 41.5) * mm, "end": v(49.25, 39.5) * mm});
            skPoint(sketch, "E12.7.1.3", {"position": v(51.5, 27) * mm});
            skLineSegment(sketch, "E12.7.1.4", {"start": v(48.75, 41.5) * mm, "end": v(48.75, 39.5) * mm});
            skLineSegment(sketch, "E12.7.1.5", {"start": v(51.5, 39.5) * mm, "end": v(46.5, 39.5) * mm});
            skPoint(sketch, "E12.7.1.6", {"position": v(49, 27) * mm});
            skLineSegment(sketch, "E12.7.1.7", {"start": v(51.5, 14.5) * mm, "end": v(46.5, 14.5) * mm});
            skLineSegment(sketch, "E12.7.1.8", {"start": v(53.5, 26.75) * mm, "end": v(51.5, 26.75) * mm});
            skPoint(sketch, "E12.7.1.9", {"position": v(53.5, 27) * mm});
            skLineSegment(sketch, "E12.7.1.10", {"start": v(46.5, 14.5) * mm, "end": v(46.5, 39.5) * mm});
            skPoint(sketch, "E12.7.1.11", {"position": v(49, 39.5) * mm});
            skPoint(sketch, "E12.7.1.12", {"position": v(49, 41.5) * mm});
            skPoint(sketch, "E12.7.1.13", {"position": v(53.5, 27) * mm});
            skPoint(sketch, "E12.7.1.14", {"position": v(49, 41.5) * mm});
            skPoint(sketch, "E12.7.1.15", {"position": v(51.5, 27) * mm});
            skLineSegment(sketch, "E12.7.1.16", {"start": v(49.25, 41.5) * mm, "end": v(48.75, 41.5) * mm});
            skLineSegment(sketch, "E12.7.1.17", {"start": v(53.5, 26.75) * mm, "end": v(53.5, 27.25) * mm});
            skLineSegment(sketch, "E12.7.1.18", {"start": v(51.5, 26.75) * mm, "end": v(51.5, 27.25) * mm});
            skLineSegment(sketch, "E12.7.1.19", {"start": v(49.25, 39.5) * mm, "end": v(48.75, 39.5) * mm});
            skLineSegment(sketch, "E12.direction1", {"start": v(-2.5, -12.5) * mm, "end": v(4.5, -12.5) * mm, "construction": true});
            skLineSegment(sketch, "E12.direction2", {"start": v(-2.5, -12.5) * mm, "end": v(-2.5, 14.5) * mm, "construction": true});
            skSolve(sketch);
        }
        {
            var Q0;
            Q0 = qSketchRegion(id + "F0", true);
            extrude(context, id + "F1", {"entities" : qUnion([Q0]), "oppositeDirection" : true, "depth" : 5 * mm, "offsetDistance" : 25 * mm});
        }
        {
            var Q0;
            Q0=makeQuery(id+"F1.opExtrude","SWEPT_FACE",FACE,{"disambiguationData":[OSD([sQuery(id+"F0.wireOp",EDGE,"E9")])]});
            var sketch = newSketch(context, id + "F2", { "sketchPlane" : qUnion([Q0])});
            skLineSegment(sketch, "E13.bottom", {"start": v(2.5, -5) * mm, "end": v(4.5, -5) * mm});
            skLineSegment(sketch, "E13.top", {"start": v(2.5, -0.5) * mm, "end": v(4.5, -0.5) * mm});
            skLineSegment(sketch, "E13.left", {"start": v(2.5, -5) * mm, "end": v(2.5, -0.5) * mm});
            skLineSegment(sketch, "E13.right", {"start": v(4.5, -5) * mm, "end": v(4.5, -0.5) * mm});
            skLineSegment(sketch, "E14.1.0.0", {"start": v(9.5, -5) * mm, "end": v(11.5, -5) * mm});
            skLineSegment(sketch, "E14.1.0.1", {"start": v(9.5, -5) * mm, "end": v(9.5, -0.5) * mm});
            skLineSegment(sketch, "E14.1.0.2", {"start": v(11.5, -5) * mm, "end": v(11.5, -0.5) * mm});
            skLineSegment(sketch, "E14.1.0.3", {"start": v(9.5, -0.5) * mm, "end": v(11.5, -0.5) * mm});
            skLineSegment(sketch, "E14.2.0.0", {"start": v(16.5, -5) * mm, "end": v(18.5, -5) * mm});
            skLineSegment(sketch, "E14.2.0.1", {"start": v(16.5, -5) * mm, "end": v(16.5, -0.5) * mm});
            skLineSegment(sketch, "E14.2.0.2", {"start": v(18.5, -5) * mm, "end": v(18.5, -0.5) * mm});
            skLineSegment(sketch, "E14.2.0.3", {"start": v(16.5, -0.5) * mm, "end": v(18.5, -0.5) * mm});
            skLineSegment(sketch, "E14.3.0.0", {"start": v(23.5, -5) * mm, "end": v(25.5, -5) * mm});
            skLineSegment(sketch, "E14.3.0.1", {"start": v(23.5, -5) * mm, "end": v(23.5, -0.5) * mm});
            skLineSegment(sketch, "E14.3.0.2", {"start": v(25.5, -5) * mm, "end": v(25.5, -0.5) * mm});
            skLineSegment(sketch, "E14.3.0.3", {"start": v(23.5, -0.5) * mm, "end": v(25.5, -0.5) * mm});
            skLineSegment(sketch, "E14.4.0.0", {"start": v(30.5, -5) * mm, "end": v(32.5, -5) * mm});
            skLineSegment(sketch, "E14.4.0.1", {"start": v(30.5, -5) * mm, "end": v(30.5, -0.5) * mm});
            skLineSegment(sketch, "E14.4.0.2", {"start": v(32.5, -5) * mm, "end": v(32.5, -0.5) * mm});
            skLineSegment(sketch, "E14.4.0.3", {"start": v(30.5, -0.5) * mm, "end": v(32.5, -0.5) * mm});
            skLineSegment(sketch, "E14.5.0.0", {"start": v(37.5, -5) * mm, "end": v(39.5, -5) * mm});
            skLineSegment(sketch, "E14.5.0.1", {"start": v(37.5, -5) * mm, "end": v(37.5, -0.5) * mm});
            skLineSegment(sketch, "E14.5.0.2", {"start": v(39.5, -5) * mm, "end": v(39.5, -0.5) * mm});
            skLineSegment(sketch, "E14.5.0.3", {"start": v(37.5, -0.5) * mm, "end": v(39.5, -0.5) * mm});
            skLineSegment(sketch, "E14.6.0.0", {"start": v(44.5, -5) * mm, "end": v(46.5, -5) * mm});
            skLineSegment(sketch, "E14.6.0.1", {"start": v(44.5, -5) * mm, "end": v(44.5, -0.5) * mm});
            skLineSegment(sketch, "E14.6.0.2", {"start": v(46.5, -5) * mm, "end": v(46.5, -0.5) * mm});
            skLineSegment(sketch, "E14.6.0.3", {"start": v(44.5, -0.5) * mm, "end": v(46.5, -0.5) * mm});
            skLineSegment(sketch, "E14.7.0.0", {"start": v(51.5, -5) * mm, "end": v(53.5, -5) * mm});
            skLineSegment(sketch, "E14.7.0.1", {"start": v(51.5, -5) * mm, "end": v(51.5, -0.5) * mm});
            skLineSegment(sketch, "E14.7.0.2", {"start": v(53.5, -5) * mm, "end": v(53.5, -0.5) * mm});
            skLineSegment(sketch, "E14.7.0.3", {"start": v(51.5, -0.5) * mm, "end": v(53.5, -0.5) * mm});
            skLineSegment(sketch, "E14.direction1", {"start": v(2.5, -5) * mm, "end": v(9.5, -5) * mm, "construction": true});
            skLineSegment(sketch, "E15.bottom", {"start": v(53.5, -0.5) * mm, "end": v(51.5, -0.5) * mm});
            skLineSegment(sketch, "E15.top", {"start": v(53.5, 0) * mm, "end": v(51.5, 0) * mm});
            skLineSegment(sketch, "E15.left", {"start": v(53.5, -0.5) * mm, "end": v(53.5, 0) * mm});
            skLineSegment(sketch, "E15.right", {"start": v(51.5, -0.5) * mm, "end": v(51.5, 0) * mm});
            skSolve(sketch);
        }
        {
            var Q0;
            Q0 = qSketchRegion(id + "F2", true);
            extrude(context, id + "F3", {"entities" : qUnion([Q0]), "operationType" : NewBodyOperationType.REMOVE, "endBound" : BoundingType.THROUGH_ALL, "oppositeDirection" : true, "depth" : 25 * mm, "offsetDistance" : 25 * mm});
        }
        {
            var Q0;
            Q0=makeQuery(id+"F1.opExtrude","SWEPT_FACE",FACE,{"disambiguationData":[OSD([sQuery(id+"F0.wireOp",EDGE,"E12.7.1.2")])]});
            var sketch = newSketch(context, id + "F4", { "sketchPlane" : qUnion([Q0])});
            skLineSegment(sketch, "E16.bottom", {"start": v(5, 41.5) * mm, "end": v(0.5, 41.5) * mm});
            skLineSegment(sketch, "E16.top", {"start": v(5, 39.5) * mm, "end": v(0.5, 39.5) * mm});
            skLineSegment(sketch, "E16.left", {"start": v(5, 41.5) * mm, "end": v(5, 39.5) * mm});
            skLineSegment(sketch, "E16.right", {"start": v(0.5, 41.5) * mm, "end": v(0.5, 39.5) * mm});
            skLineSegment(sketch, "E17.0.1.0", {"start": v(5, 12.5) * mm, "end": v(0.5, 12.5) * mm});
            skLineSegment(sketch, "E17.0.1.1", {"start": v(5, 14.5) * mm, "end": v(0.5, 14.5) * mm});
            skLineSegment(sketch, "E17.0.1.2", {"start": v(0.5, 14.5) * mm, "end": v(0.5, 12.5) * mm});
            skLineSegment(sketch, "E17.0.1.3", {"start": v(5, 14.5) * mm, "end": v(5, 12.5) * mm});
            skLineSegment(sketch, "E17.direction1", {"start": v(0.5, 39.5) * mm, "end": v(5.8, 39.5) * mm, "construction": true});
            skLineSegment(sketch, "E17.direction2", {"start": v(0.5, 39.5) * mm, "end": v(0.5, 12.5) * mm, "construction": true});
            skLineSegment(sketch, "E18.bottom", {"start": v(0.5, 41.5) * mm, "end": v(0, 41.5) * mm});
            skLineSegment(sketch, "E18.top", {"start": v(0.5, 39.5) * mm, "end": v(0, 39.5) * mm});
            skLineSegment(sketch, "E18.right", {"start": v(0, 41.5) * mm, "end": v(0, 39.5) * mm});
            skSolve(sketch);
        }
        {
            var Q0;
            Q0 = qSketchRegion(id + "F4", true);
            extrude(context, id + "F5", {"entities" : qUnion([Q0]), "operationType" : NewBodyOperationType.REMOVE, "endBound" : BoundingType.THROUGH_ALL, "oppositeDirection" : true, "depth" : 25 * mm, "offsetDistance" : 25 * mm});
        }
    });
